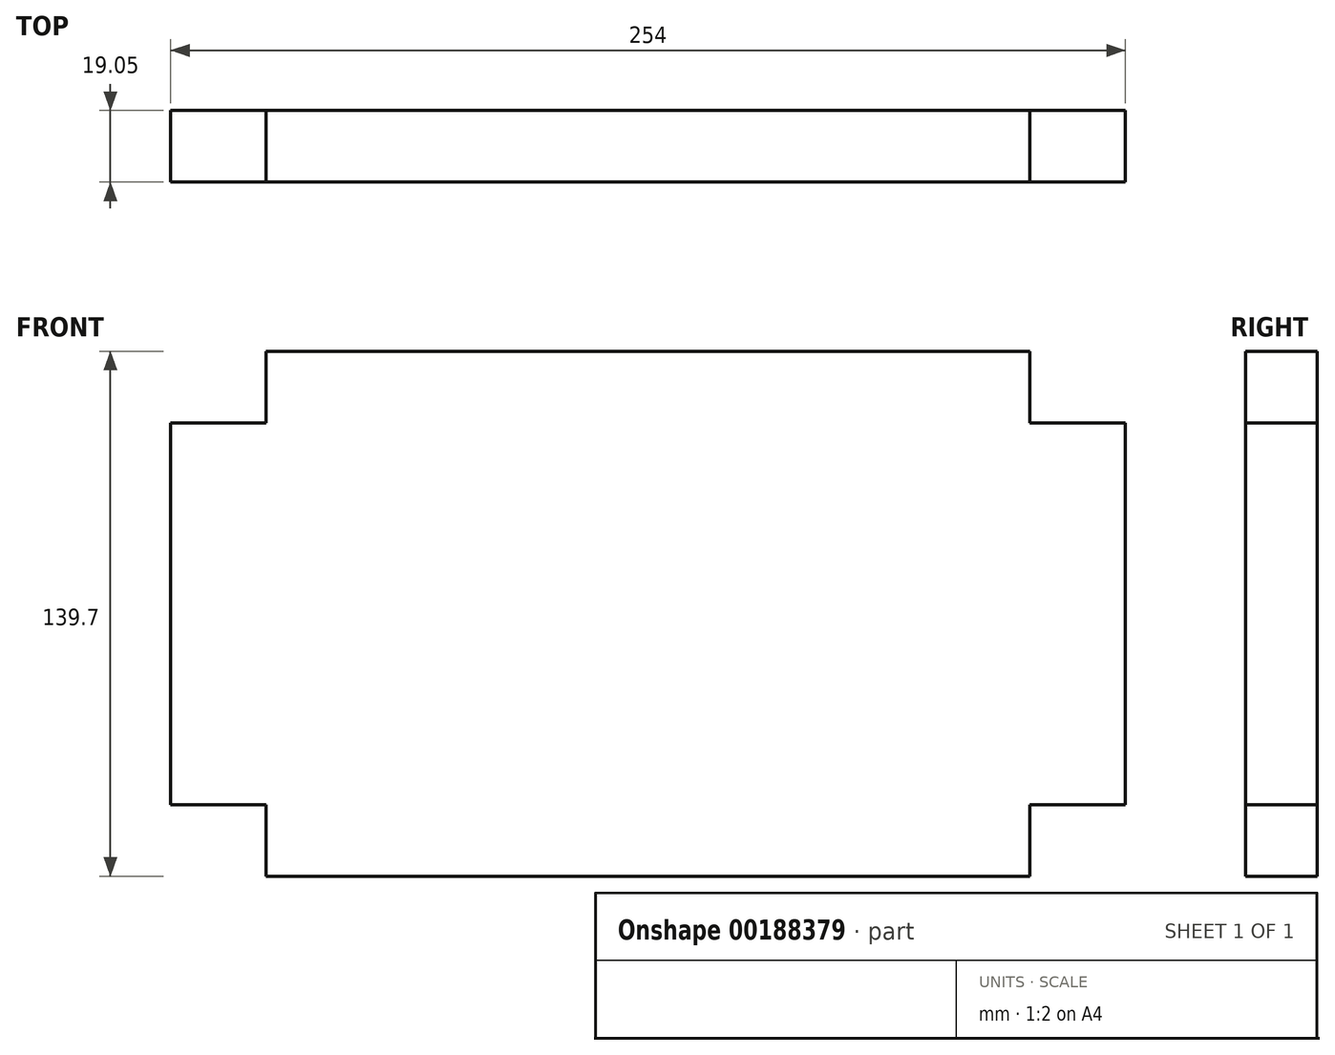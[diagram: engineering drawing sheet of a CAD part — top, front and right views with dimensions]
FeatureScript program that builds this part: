
annotation { "Feature Type Name" : "Feature", "Feature Type Description" : "" }
export const myFeature = defineFeature(function(context is Context, id is Id, definition is map)
    precondition{}
    {
        {
            var Q0;
            Q0=qCreatedBy(makeId("Front.planeOp"),FACE);
            var sketch = newSketch(context, id + "F0", { "sketchPlane" : qUnion([Q0])});
            skLineSegment(sketch, "E0.bottom", {"start": v(101.6, -69.85) * mm, "end": v(-101.6, -69.85) * mm});
            skLineSegment(sketch, "E0.top", {"start": v(101.6, 69.85) * mm, "end": v(-101.6, 69.85) * mm});
            skLineSegment(sketch, "E0.left", {"start": v(127, -50.8) * mm, "end": v(127, 50.8) * mm});
            skLineSegment(sketch, "E0.right", {"start": v(-127, -50.8) * mm, "end": v(-127, 50.8) * mm});
            skPoint(sketch, "E0.middle", {"position": v(0, 0) * mm});
            skLineSegment(sketch, "E1.0", {"start": v(127, 50.8) * mm, "end": v(101.6, 50.8) * mm});
            skLineSegment(sketch, "E2", {"start": v(0, 0) * mm, "end": v(0, -34.96) * mm, "construction": true});
            skLineSegment(sketch, "E3", {"start": v(0, 0) * mm, "end": v(-27.68, 0) * mm, "construction": true});
            skLineSegment(sketch, "E4.0", {"start": v(-101.6, 69.85) * mm, "end": v(-101.6, 50.8) * mm});
            skLineSegment(sketch, "E5.MirrorCS", {"start": v(101.6, 69.85) * mm, "end": v(101.6, 50.8) * mm});
            skLineSegment(sketch, "E6.trimOffspring", {"start": v(-101.6, 50.8) * mm, "end": v(-127, 50.8) * mm});
            skLineSegment(sketch, "E7.MirrorCS", {"start": v(-101.6, -50.8) * mm, "end": v(-127, -50.8) * mm});
            skLineSegment(sketch, "E8.MirrorCS", {"start": v(-101.6, -69.85) * mm, "end": v(-101.6, -50.8) * mm});
            skLineSegment(sketch, "E9.MirrorCS", {"start": v(101.6, -69.85) * mm, "end": v(101.6, -50.8) * mm});
            skLineSegment(sketch, "E10.MirrorCS", {"start": v(127, -50.8) * mm, "end": v(101.6, -50.8) * mm});
            skLineSegment(sketch, "E11.MirrorCS", {"start": v(127, 69.85) * mm, "end": v(-101.6, 69.85) * mm});
            skPoint(sketch, "E12.orphan", {"position": v(-127, -69.85) * mm});
            skPoint(sketch, "E13.orphan", {"position": v(127, -69.85) * mm});
            skPoint(sketch, "E14.orphan", {"position": v(127, 69.85) * mm});
            skPoint(sketch, "E15.orphan", {"position": v(-127, 69.85) * mm});
            skSolve(sketch);
        }
        {
            var Q0;
            Q0 = qSketchRegion(id + "F0", true);
            extrude(context, id + "F1", {"entities" : qUnion([Q0]), "depth" : 19.05 * mm});
        }
    });
